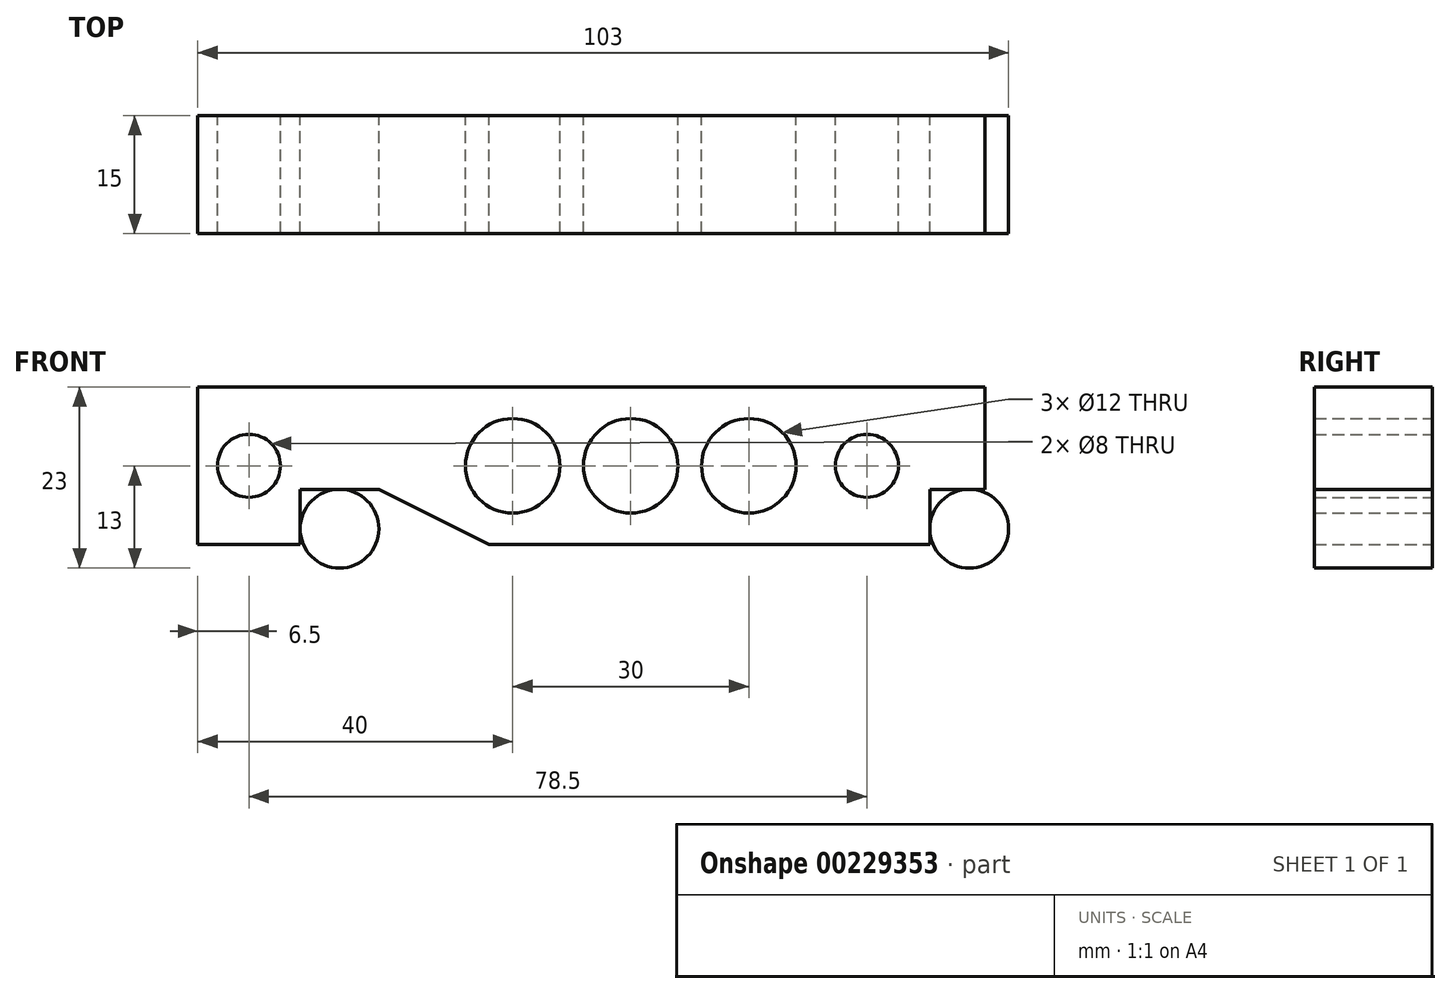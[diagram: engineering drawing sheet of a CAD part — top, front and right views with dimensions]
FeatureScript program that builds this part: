
annotation { "Feature Type Name" : "Feature", "Feature Type Description" : "" }
export const myFeature = defineFeature(function(context is Context, id is Id, definition is map)
    precondition{}
    {
        {
            var Q0;
            Q0=qCreatedBy(makeId("Front.planeOp"),FACE);
            var sketch = newSketch(context, id + "F0", { "sketchPlane" : qUnion([Q0])});
            skLineSegment(sketch, "E0.bottom", {"start": v(43, -10) * mm, "end": v(-13, -10) * mm});
            skLineSegment(sketch, "E0.top", {"start": v(50, 10) * mm, "end": v(-50, 10) * mm});
            skLineSegment(sketch, "E0.left", {"start": v(50, -3) * mm, "end": v(50, 10) * mm});
            skLineSegment(sketch, "E0.right", {"start": v(-50, -10) * mm, "end": v(-50, 10) * mm});
            skPoint(sketch, "E0.middle", {"position": v(0, 0) * mm});
            skLineSegment(sketch, "E1", {"start": v(50, -3) * mm, "end": v(43, -3) * mm});
            skLineSegment(sketch, "E2", {"start": v(43, -3) * mm, "end": v(43, -10) * mm});
            skPoint(sketch, "E3", {"position": v(-37, -3) * mm});
            skLineSegment(sketch, "E4", {"start": v(-37, -3) * mm, "end": v(-37, -10) * mm});
            skLineSegment(sketch, "E5", {"start": v(-37, -3) * mm, "end": v(-27, -3) * mm});
            skLineSegment(sketch, "E6", {"start": v(-27, -3) * mm, "end": v(-13, -10) * mm});
            skLineSegment(sketch, "E7", {"start": v(-27, -3) * mm, "end": v(-20, -3) * mm, "construction": true});
            skLineSegment(sketch, "E8", {"start": v(-13, -3) * mm, "end": v(-13, -10) * mm, "construction": true});
            skLineSegment(sketch, "E9", {"start": v(-20, -3) * mm, "end": v(-13, -3) * mm, "construction": true});
            skLineSegment(sketch, "E10.trimOffspring", {"start": v(-37, -10) * mm, "end": v(-50, -10) * mm});
            skCircle(sketch, "E11", {"center": v(-43.5, 0) * mm, "radius": 4 * mm});
            skCircle(sketch, "E12", {"center": v(35, 0) * mm, "radius": 4 * mm});
            skLineSegment(sketch, "E13", {"start": v(-37, -3) * mm, "end": v(-50, -3) * mm, "construction": true});
            skLineSegment(sketch, "E14", {"start": v(-43.5, -3) * mm, "end": v(-43.5, 0) * mm, "construction": true});
            skCircle(sketch, "E15", {"center": v(-32, -8) * mm, "radius": 5 * mm});
            skCircle(sketch, "E16", {"center": v(48, -8) * mm, "radius": 5 * mm});
            skCircle(sketch, "E17", {"center": v(20, 0) * mm, "radius": 6 * mm});
            skCircle(sketch, "E18.1.0.0", {"center": v(5, 0) * mm, "radius": 6 * mm});
            skCircle(sketch, "E18.2.0.0", {"center": v(-10, 0) * mm, "radius": 6 * mm});
            skLineSegment(sketch, "E18.direction1", {"start": v(20, 0) * mm, "end": v(5, 0) * mm, "construction": true});
            skSolve(sketch);
        }
        {
            var Q0;
            Q0=makeQuery(id+"F0.imprint","IMPRINT",FACE,{"disambiguationData":[TD([[makeQuery(id+"F0.imprint","IMPRINT",EDGE,{"derivedFrom":sQuery(id+"F0.wireOp",EDGE,"E0.bottom")}),-1.0]])]});
            var Q1;
            {var subQ0=sQuery(id+"F0.wireOp",EDGE,"E15");var subQ1=makeQuery(id+"F0.imprint","INTERSECT",VERTEX,{"derivedFrom":[sQuery(id+"F0.wireOp",EDGE,"E4"),subQ0]});Q1=makeQuery(id+"F0.imprint","IMPRINT",FACE,{"disambiguationData":[TD([[makeQuery(id+"F0.imprint","IMPRINT",EDGE,{"disambiguationData":[TD([[subQ1,1.0]])],"derivedFrom":subQ0}),1.0]])]});}
            var Q2;
            {var subQ0=sQuery(id+"F0.wireOp",EDGE,"E16");var subQ1=makeQuery(id+"F0.imprint","INTERSECT",VERTEX,{"derivedFrom":[sQuery(id+"F0.wireOp",EDGE,"E1"),subQ0]});Q2=makeQuery(id+"F0.imprint","IMPRINT",FACE,{"disambiguationData":[TD([[makeQuery(id+"F0.imprint","IMPRINT",EDGE,{"disambiguationData":[TD([[subQ1,-1.0]])],"derivedFrom":subQ0}),1.0]])]});}
            extrude(context, id + "F1", {"entities" : qUnion([Q0, Q1, Q2]), "depth" : 15 * mm});
        }
    });
